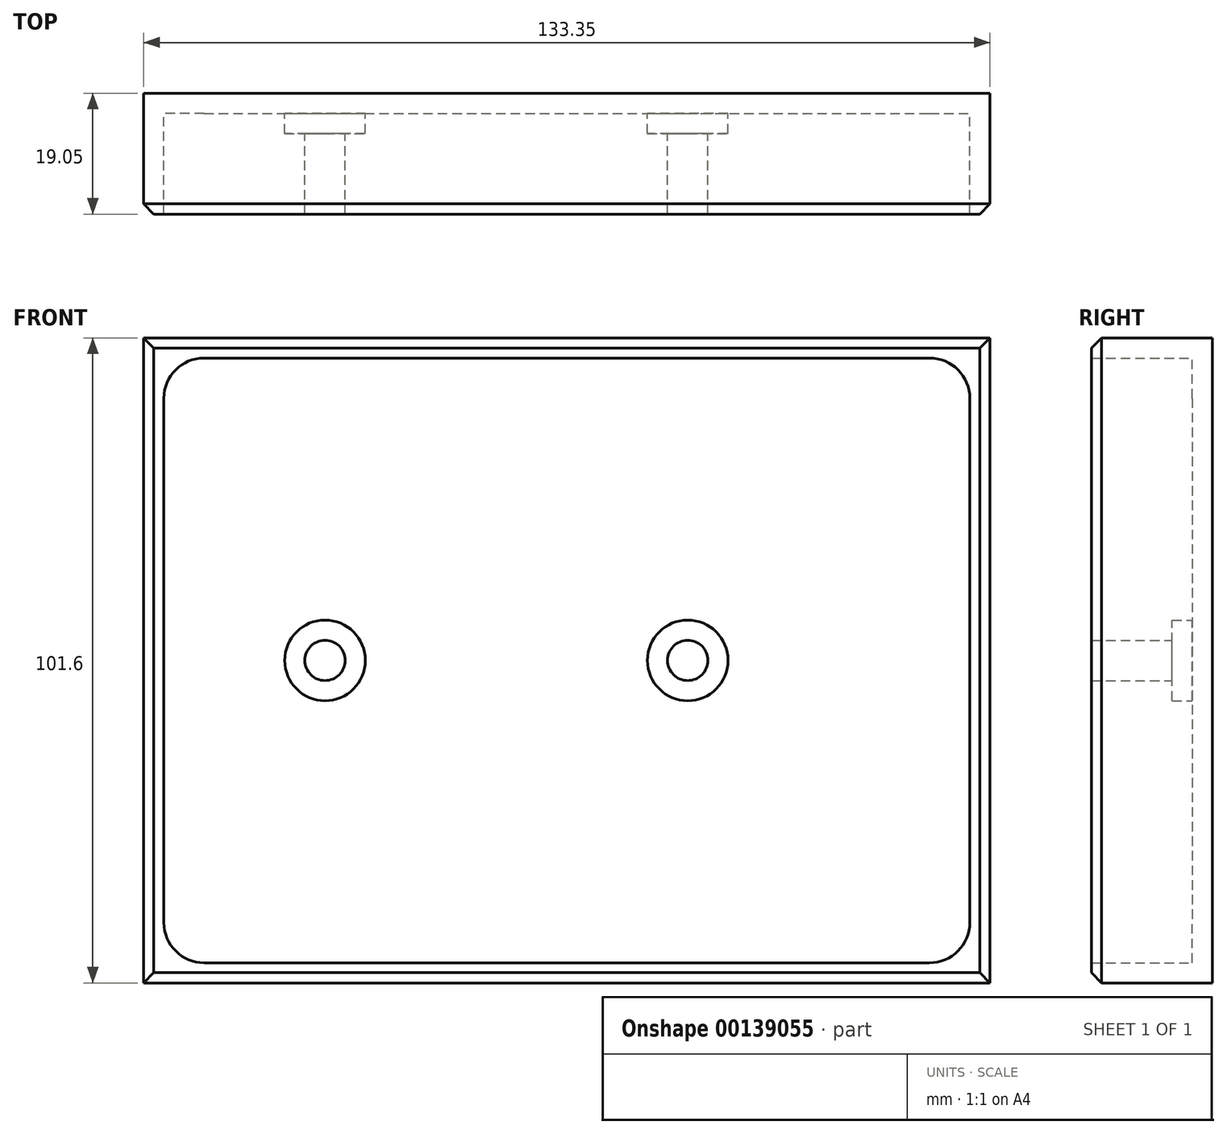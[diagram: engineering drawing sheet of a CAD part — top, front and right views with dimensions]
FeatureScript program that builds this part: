
annotation { "Feature Type Name" : "Feature", "Feature Type Description" : "" }
export const myFeature = defineFeature(function(context is Context, id is Id, definition is map)
    precondition{}
    {
        {
            var Q0;
            Q0=qCreatedBy(makeId("Front.planeOp"),FACE);
            var sketch = newSketch(context, id + "F0", { "sketchPlane" : qUnion([Q0])});
            skLineSegment(sketch, "E0.bottom", {"start": v(0, 0) * mm, "end": v(133.35, 0) * mm});
            skLineSegment(sketch, "E0.top", {"start": v(0, -101.6) * mm, "end": v(133.35, -101.6) * mm});
            skLineSegment(sketch, "E0.left", {"start": v(0, 0) * mm, "end": v(0, -101.6) * mm});
            skLineSegment(sketch, "E0.right", {"start": v(133.35, 0) * mm, "end": v(133.35, -101.6) * mm});
            skSolve(sketch);
        }
        {
            var Q0;
            Q0 = qSketchRegion(id + "F0", true);
            extrude(context, id + "F1", {"entities" : qUnion([Q0]), "depth" : 19.05 * mm});
        }
        {
            var Q0;
            Q0=makeQuery(id+"F1.opExtrude","CAP_FACE",FACE,{"disambiguationData":[OSD([sQuery(id+"F0.wireOp",EDGE,"E0.bottom"),sQuery(id+"F0.wireOp",EDGE,"E0.top"),sQuery(id+"F0.wireOp",EDGE,"E0.left"),sQuery(id+"F0.wireOp",EDGE,"E0.right")])],"isStart":false});
            shell(context, id + "F2", {"entities" : qUnion([Q0]), "thickness" : 3.17 * mm});
        }
        {
            var Q0;
            Q0=makeQuery(id+"F2.opShell","OFFSET_FACE",FACE,{"disambiguationData":[OSD([sQuery(id+"F0.wireOp",EDGE,"E0.bottom"),sQuery(id+"F0.wireOp",EDGE,"E0.top"),sQuery(id+"F0.wireOp",EDGE,"E0.left"),sQuery(id+"F0.wireOp",EDGE,"E0.right")])]});
            var sketch = newSketch(context, id + "F3", { "sketchPlane" : qUnion([Q0])});
            skCircle(sketch, "E1", {"center": v(28.58, -50.8) * mm, "radius": 6.35 * mm});
            skPoint(sketch, "E1.centerSnap0", {"position": v(3.17, -50.8) * mm});
            skCircle(sketch, "E2", {"center": v(85.73, -50.8) * mm, "radius": 6.35 * mm});
            skSolve(sketch);
        }
        {
            var Q0;
            Q0 = qSketchRegion(id + "F3", true);
            extrude(context, id + "F4", {"entities" : qUnion([Q0]), "operationType" : NewBodyOperationType.ADD, "depth" : 3.17 * mm});
        }
        {
            var Q0;
            Q0=makeQuery(id+"F4.opExtrude","CAP_FACE",FACE,{"disambiguationData":[OSD([sQuery(id+"F3.wireOp",EDGE,"E1")])],"isStart":false});
            var sketch = newSketch(context, id + "F5", { "sketchPlane" : qUnion([Q0])});
            skCircle(sketch, "E3", {"center": v(28.58, -50.8) * mm, "radius": 3.18 * mm});
            skSolve(sketch);
        }
        {
            var Q0;
            Q0 = qSketchRegion(id + "F5", true);
            extrude(context, id + "F6", {"entities" : qUnion([Q0]), "operationType" : NewBodyOperationType.ADD, "depth" : 12.7 * mm});
        }
        {
            var Q0;
            Q0=makeQuery(id+"F4.opExtrude","CAP_FACE",FACE,{"disambiguationData":[OSD([sQuery(id+"F3.wireOp",EDGE,"E2")])],"isStart":false});
            var sketch = newSketch(context, id + "F7", { "sketchPlane" : qUnion([Q0])});
            skCircle(sketch, "E4", {"center": v(85.73, -50.8) * mm, "radius": 3.18 * mm});
            skSolve(sketch);
        }
        {
            var Q0;
            Q0 = qSketchRegion(id + "F7", true);
            extrude(context, id + "F8", {"entities" : qUnion([Q0]), "operationType" : NewBodyOperationType.ADD, "depth" : 12.7 * mm});
        }
        {
            var Q0;
            Q0=makeQuery(id+"F2.opShell","OFFSET_EDGE",EDGE,{"disambiguationData":[OSD([sQuery(id+"F0.wireOp",EDGE,"E0.bottom"),sQuery(id+"F0.wireOp",EDGE,"E0.left")])]});
            var Q1;
            Q1=makeQuery(id+"F2.opShell","OFFSET_EDGE",EDGE,{"disambiguationData":[OSD([sQuery(id+"F0.wireOp",EDGE,"E0.bottom"),sQuery(id+"F0.wireOp",EDGE,"E0.right")])]});
            var Q2;
            Q2=makeQuery(id+"F2.opShell","OFFSET_EDGE",EDGE,{"disambiguationData":[OSD([sQuery(id+"F0.wireOp",EDGE,"E0.top"),sQuery(id+"F0.wireOp",EDGE,"E0.left")])]});
            var Q3;
            Q3=makeQuery(id+"F2.opShell","OFFSET_EDGE",EDGE,{"disambiguationData":[OSD([sQuery(id+"F0.wireOp",EDGE,"E0.top"),sQuery(id+"F0.wireOp",EDGE,"E0.right")])]});
            fillet(context, id + "F9", {"entities" : qUnion([Q0, Q1, Q2, Q3]), "radius" : 6.35 * mm, "tangentPropagation" : true, "allowEdgeOverflow" : false});
        }
        {
            var Q0;
            Q0=makeQuery(id+"F1.opExtrude","CAP_EDGE",EDGE,{"disambiguationData":[OSD([sQuery(id+"F0.wireOp",EDGE,"E0.top")])],"isStart":false});
            var Q1;
            Q1=makeQuery(id+"F1.opExtrude","CAP_EDGE",EDGE,{"disambiguationData":[OSD([sQuery(id+"F0.wireOp",EDGE,"E0.right")])],"isStart":false});
            var Q2;
            Q2=makeQuery(id+"F1.opExtrude","CAP_EDGE",EDGE,{"disambiguationData":[OSD([sQuery(id+"F0.wireOp",EDGE,"E0.bottom")])],"isStart":false});
            var Q3;
            Q3=makeQuery(id+"F1.opExtrude","CAP_EDGE",EDGE,{"disambiguationData":[OSD([sQuery(id+"F0.wireOp",EDGE,"E0.left")])],"isStart":false});
            chamfer(context, id + "F10", {"entities" : qUnion([Q0, Q1, Q2, Q3]), "width" : 1.6 * mm, "tangentPropagation" : true});
        }
    });
